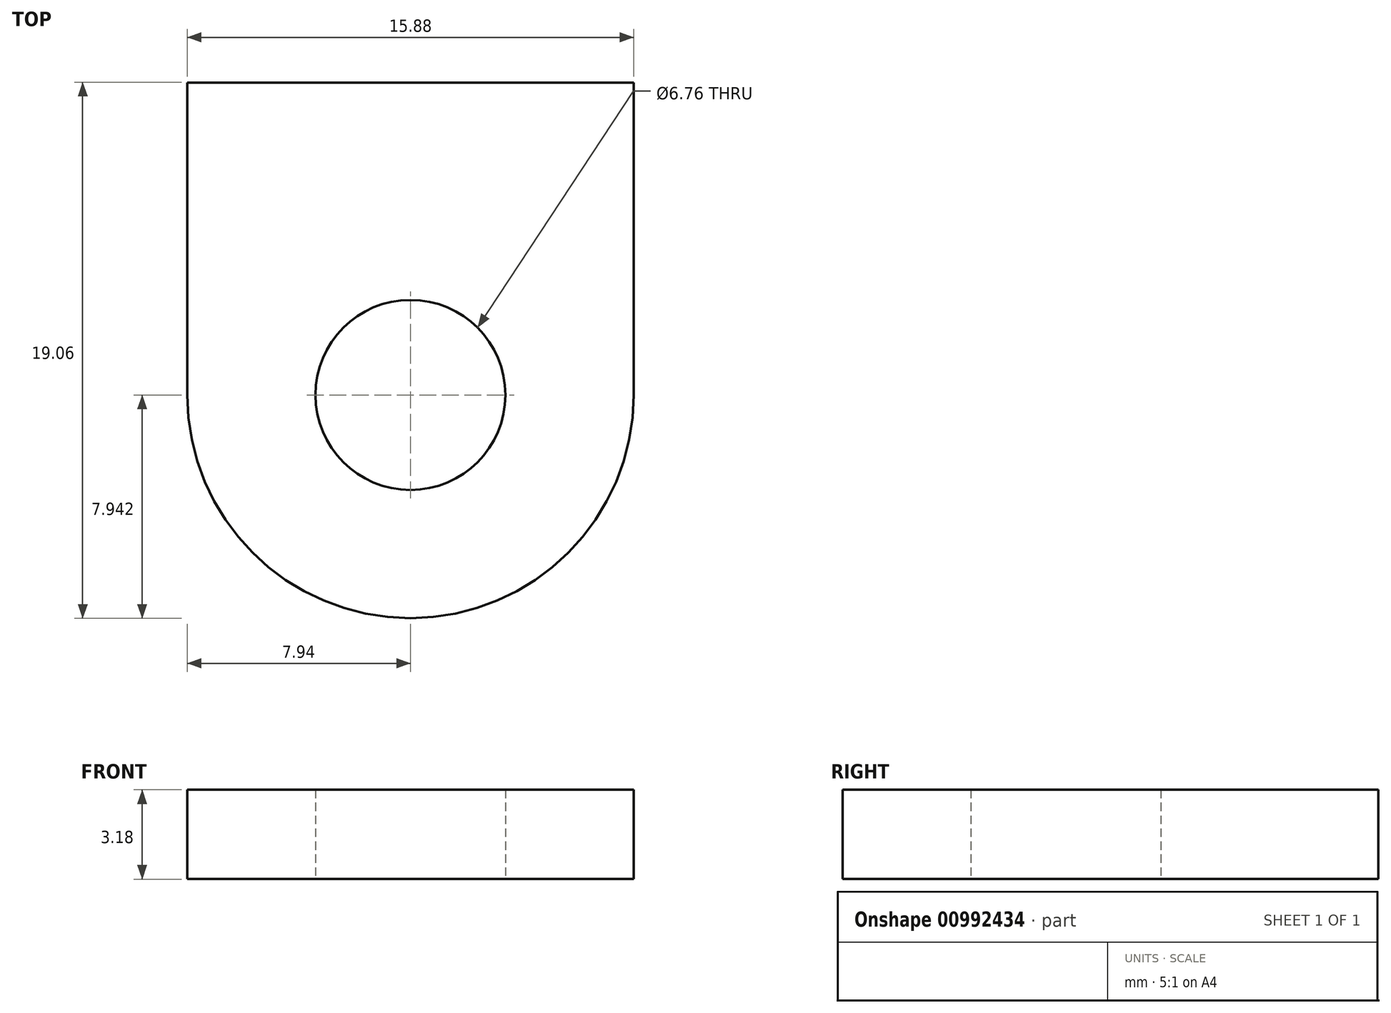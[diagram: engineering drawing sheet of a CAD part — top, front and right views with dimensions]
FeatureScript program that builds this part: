
annotation { "Feature Type Name" : "Feature", "Feature Type Description" : "" }
export const myFeature = defineFeature(function(context is Context, id is Id, definition is map)
    precondition{}
    {
        {
            var Q0;
            Q0=qCreatedBy(makeId("Top.planeOp"),FACE);
            var sketch = newSketch(context, id + "F0", { "sketchPlane" : qUnion([Q0])});
            skLineSegment(sketch, "E0.bottom", {"start": v(7.94, 9.52) * mm, "end": v(-7.94, 9.52) * mm});
            skLineSegment(sketch, "E0.left", {"start": v(7.94, 9.53) * mm, "end": v(7.94, -1.59) * mm});
            skLineSegment(sketch, "E0.right", {"start": v(-7.94, 9.53) * mm, "end": v(-7.94, -1.59) * mm});
            skPoint(sketch, "E0.middle", {"position": v(0, 0) * mm});
            skCircle(sketch, "E1", {"center": v(0, -1.59) * mm, "radius": 3.57 * mm});
            skArc(sketch, "E2", {"start": v(-7.94, -1.59) * mm, "mid": v(0, -9.53) * mm, "end": v(7.94, -1.59) * mm});
            skSolve(sketch);
        }
        {
            var Q0;
            Q0=makeQuery(id+"F0.imprint","IMPRINT",FACE,{"disambiguationData":[TD([[makeQuery(id+"F0.imprint","IMPRINT",EDGE,{"derivedFrom":sQuery(id+"F0.wireOp",EDGE,"E0.bottom")}),1.0]])]});
            var Q1;
            Q1=makeQuery(id+"F0.imprint","IMPRINT",FACE,{"disambiguationData":[TD([[makeQuery(id+"F0.imprint","IMPRINT",EDGE,{"derivedFrom":sQuery(id+"F0.wireOp",EDGE,"E1")}),1.0]])]});
            extrude(context, id + "F1", {"entities" : qUnion([Q0, Q1]), "oppositeDirection" : true, "depth" : 3.17 * mm, "offsetDistance" : 25.4 * mm});
        }
        {
            var Q0;
            Q0=sQuery(id+"F0.wireOp",VERTEX,"E1.center");
            var Q1;
            Q1=makeQuery(id+"F1.opExtrude","SWEPT_BODY",BODY,{"disambiguationData":[OSD([sQuery(id+"F0.wireOp",EDGE,"E0.bottom"),sQuery(id+"F0.wireOp",EDGE,"E0.left"),sQuery(id+"F0.wireOp",EDGE,"E0.right"),sQuery(id+"F0.wireOp",EDGE,"E2")])]});
            hole(context, id + "F2", {"style" : HoleStyle.SIMPLE, "endStyle" : HoleEndStyle.THROUGH, "standardTappedOrClearance" : lookupTablePath({ "fit" : "Close (ASME)", "standard" : "ANSI", "size" : "1/4", "type" : "Clearance" }), "standardBlindInLast" : lookupTablePath({ "fit" : "Close", "standard" : "ANSI", "engagement" : "75%", "pitch" : "20 tpi", "size" : "1/4", "type" : "Clearance & tapped" }), "holeDiameter" : 6.76 * mm, "majorDiameter" : 6.35 * mm, "isTappedThrough" : true, "tappedDepth" : 12.7 * mm, "tapClearance" : 3, "locations" : qUnion([Q0]), "scope" : qUnion([Q1]), "startStyle" : HoleStartStyle.SKETCH});
        }
    });
